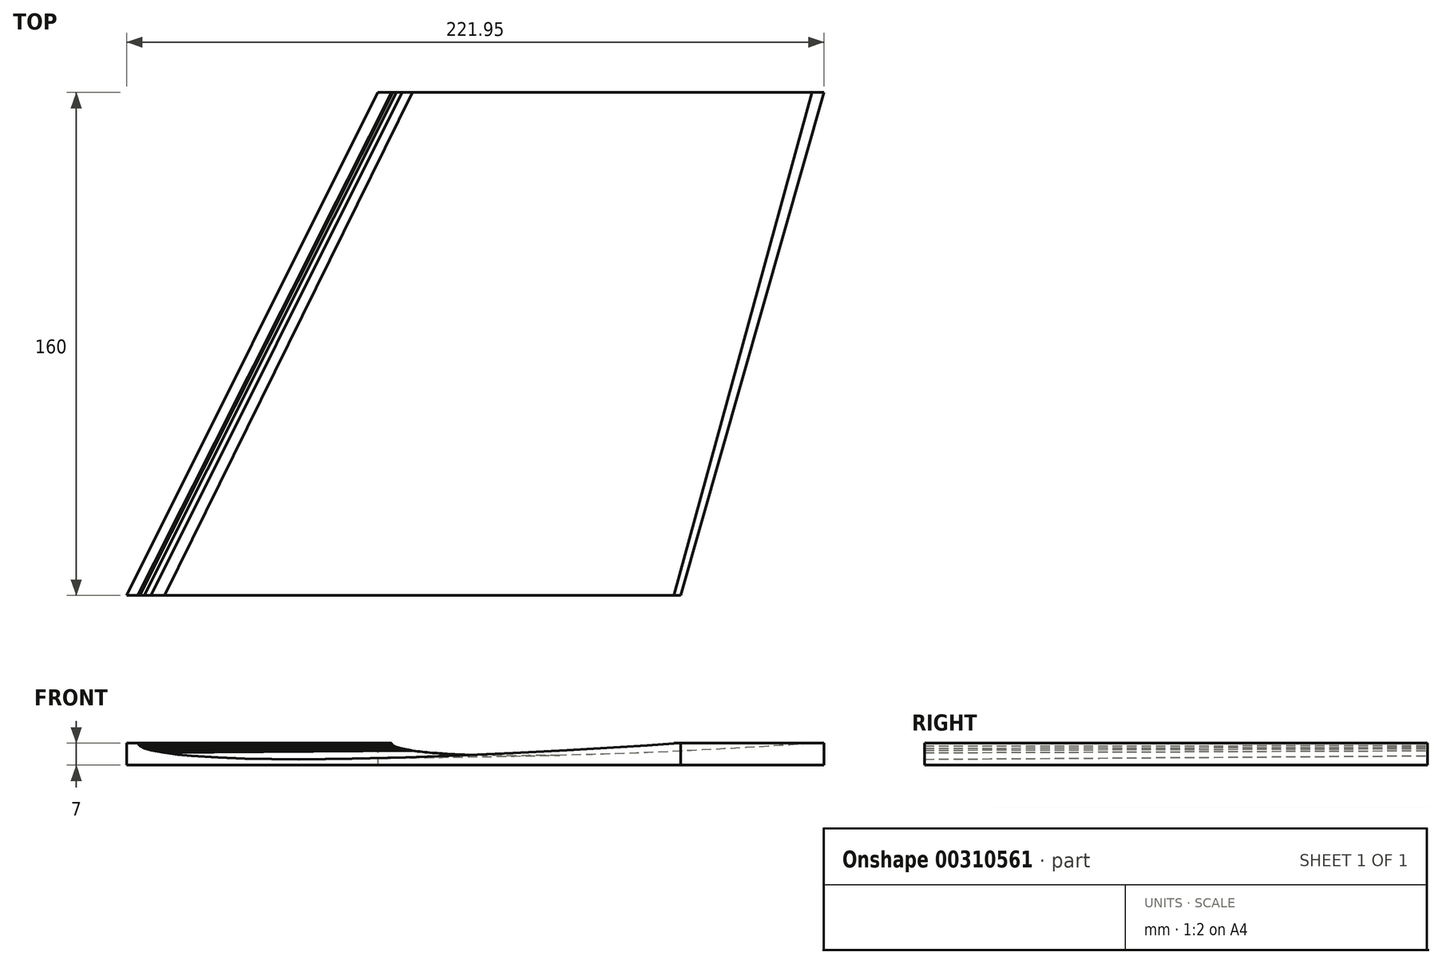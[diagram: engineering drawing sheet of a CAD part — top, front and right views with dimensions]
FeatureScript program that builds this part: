
annotation { "Feature Type Name" : "Feature", "Feature Type Description" : "" }
export const myFeature = defineFeature(function(context is Context, id is Id, definition is map)
    precondition{}
    {
        {
            var Q0;
            Q0=qCreatedBy(makeId("Front.planeOp"),FACE);
            cPlane(context, id + "F0", {"entities" : qUnion([Q0]), "cplaneType" : CPlaneType.OFFSET, "offset" : 242 * mm, "oppositeDirection" : true, "width" : 150 * mm, "height" : 150 * mm});
        }
        {
            var Q0;
            Q0=qCreatedBy(makeId("Front.planeOp"),FACE);
            cPlane(context, id + "F1", {"entities" : qUnion([Q0]), "cplaneType" : CPlaneType.OFFSET, "offset" : 315 * mm, "oppositeDirection" : true, "width" : 150 * mm, "height" : 150 * mm});
        }
        {
            var Q0;
            Q0=qCreatedBy(makeId("Front.planeOp"),FACE);
            var sketch = newSketch(context, id + "F2", { "sketchPlane" : qUnion([Q0])});
            skLineSegment(sketch, "E0", {"start": v(85.33, 0.1) * mm, "end": v(76.8, 0.69) * mm});
            skLineSegment(sketch, "E1", {"start": v(76.8, 0.69) * mm, "end": v(68.27, 1.23) * mm});
            skLineSegment(sketch, "E2", {"start": v(68.27, 1.23) * mm, "end": v(51.2, 2.24) * mm});
            skLineSegment(sketch, "E3", {"start": v(51.2, 2.24) * mm, "end": v(34.13, 3.12) * mm});
            skLineSegment(sketch, "E4", {"start": v(34.13, 3.12) * mm, "end": v(17.07, 3.9) * mm});
            skLineSegment(sketch, "E5", {"start": v(17.07, 3.9) * mm, "end": v(0, 4.51) * mm});
            skLineSegment(sketch, "E6", {"start": v(0, 4.51) * mm, "end": v(-17.07, 4.95) * mm});
            skLineSegment(sketch, "E7", {"start": v(-17.07, 4.95) * mm, "end": v(-34.13, 5.12) * mm});
            skLineSegment(sketch, "E8", {"start": v(-34.13, 5.12) * mm, "end": v(-42.67, 5.07) * mm});
            skLineSegment(sketch, "E9", {"start": v(-42.67, 5.07) * mm, "end": v(-51.2, 4.9) * mm});
            skLineSegment(sketch, "E10", {"start": v(-51.2, 4.9) * mm, "end": v(-59.73, 4.56) * mm});
            skLineSegment(sketch, "E11", {"start": v(-59.73, 4.56) * mm, "end": v(-68.27, 4) * mm});
            skLineSegment(sketch, "E12", {"start": v(-68.27, 4) * mm, "end": v(-72.53, 3.58) * mm});
            skLineSegment(sketch, "E13", {"start": v(-72.53, 3.58) * mm, "end": v(-76.8, 3.03) * mm});
            skLineSegment(sketch, "E14", {"start": v(-76.8, 3.03) * mm, "end": v(-81.07, 2.23) * mm});
            skLineSegment(sketch, "E15", {"start": v(-81.07, 2.23) * mm, "end": v(-83.2, 1.62) * mm});
            skLineSegment(sketch, "E16", {"start": v(-83.2, 1.62) * mm, "end": v(-84.61, 0.9) * mm});
            skLineSegment(sketch, "E17", {"start": v(-84.61, 0.9) * mm, "end": v(-85.33, 0) * mm});
            skLineSegment(sketch, "E18", {"start": v(-85.33, 0) * mm, "end": v(-84.68, -0.91) * mm});
            skLineSegment(sketch, "E19", {"start": v(-84.68, -0.91) * mm, "end": v(-83.2, -1.62) * mm});
            skLineSegment(sketch, "E20", {"start": v(-83.2, -1.62) * mm, "end": v(-81.07, -2.23) * mm});
            skLineSegment(sketch, "E21", {"start": v(-81.07, -2.23) * mm, "end": v(-76.8, -3.03) * mm});
            skLineSegment(sketch, "E22", {"start": v(-76.8, -3.03) * mm, "end": v(-72.53, -3.58) * mm});
            skLineSegment(sketch, "E23", {"start": v(-72.53, -3.58) * mm, "end": v(-68.27, -4) * mm});
            skLineSegment(sketch, "E24", {"start": v(-68.27, -4) * mm, "end": v(-59.73, -4.56) * mm});
            skLineSegment(sketch, "E25", {"start": v(-59.73, -4.56) * mm, "end": v(-51.2, -4.9) * mm});
            skLineSegment(sketch, "E26", {"start": v(-51.2, -4.9) * mm, "end": v(-42.67, -5.07) * mm});
            skLineSegment(sketch, "E27", {"start": v(-42.67, -5.07) * mm, "end": v(-34.13, -5.12) * mm});
            skLineSegment(sketch, "E28", {"start": v(-34.13, -5.12) * mm, "end": v(-17.07, -4.95) * mm});
            skLineSegment(sketch, "E29", {"start": v(-17.07, -4.95) * mm, "end": v(0, -4.51) * mm});
            skLineSegment(sketch, "E30", {"start": v(0, -4.51) * mm, "end": v(17.07, -3.9) * mm});
            skLineSegment(sketch, "E31", {"start": v(17.07, -3.9) * mm, "end": v(34.13, -3.12) * mm});
            skLineSegment(sketch, "E32", {"start": v(34.13, -3.12) * mm, "end": v(51.2, -2.24) * mm});
            skLineSegment(sketch, "E33", {"start": v(51.2, -2.24) * mm, "end": v(68.27, -1.23) * mm});
            skLineSegment(sketch, "E34", {"start": v(68.27, -1.23) * mm, "end": v(76.8, -0.69) * mm});
            skLineSegment(sketch, "E35", {"start": v(76.8, -0.69) * mm, "end": v(85.33, -0.1) * mm});
            skLineSegment(sketch, "E36", {"start": v(85.33, -0.1) * mm, "end": v(85.33, 0.1) * mm});
            skSolve(sketch);
        }
        {
            var Q0;
            Q0=qCreatedBy(id+"F0.planeOp",FACE);
            var sketch = newSketch(context, id + "F3", { "sketchPlane" : qUnion([Q0])});
            skLineSegment(sketch, "E37", {"start": v(151.77, 0.06) * mm, "end": v(146.02, 0.44) * mm});
            skLineSegment(sketch, "E38", {"start": v(146.02, 0.44) * mm, "end": v(140.27, 0.8) * mm});
            skLineSegment(sketch, "E39", {"start": v(140.27, 0.8) * mm, "end": v(128.77, 1.48) * mm});
            skLineSegment(sketch, "E40", {"start": v(128.77, 1.48) * mm, "end": v(117.27, 2.07) * mm});
            skLineSegment(sketch, "E41", {"start": v(117.27, 2.07) * mm, "end": v(105.77, 2.58) * mm});
            skLineSegment(sketch, "E42", {"start": v(105.77, 2.58) * mm, "end": v(94.27, 3) * mm});
            skLineSegment(sketch, "E43", {"start": v(94.27, 3) * mm, "end": v(82.77, 3.28) * mm});
            skLineSegment(sketch, "E44", {"start": v(82.77, 3.28) * mm, "end": v(71.27, 3.4) * mm});
            skLineSegment(sketch, "E45", {"start": v(71.27, 3.4) * mm, "end": v(65.52, 3.36) * mm});
            skLineSegment(sketch, "E46", {"start": v(65.52, 3.36) * mm, "end": v(59.77, 3.24) * mm});
            skLineSegment(sketch, "E47", {"start": v(59.77, 3.24) * mm, "end": v(54.02, 3.02) * mm});
            skLineSegment(sketch, "E48", {"start": v(54.02, 3.02) * mm, "end": v(48.27, 2.64) * mm});
            skLineSegment(sketch, "E49", {"start": v(48.27, 2.64) * mm, "end": v(45.4, 2.37) * mm});
            skLineSegment(sketch, "E50", {"start": v(45.4, 2.37) * mm, "end": v(42.52, 2) * mm});
            skLineSegment(sketch, "E51", {"start": v(42.52, 2) * mm, "end": v(39.65, 1.47) * mm});
            skLineSegment(sketch, "E52", {"start": v(39.65, 1.47) * mm, "end": v(38.2, 1.06) * mm});
            skLineSegment(sketch, "E53", {"start": v(38.2, 1.06) * mm, "end": v(37.26, 0.58) * mm});
            skLineSegment(sketch, "E54", {"start": v(37.26, 0.58) * mm, "end": v(36.77, -0.01) * mm});
            skLineSegment(sketch, "E55", {"start": v(36.77, -0.01) * mm, "end": v(37.21, -0.62) * mm});
            skLineSegment(sketch, "E56", {"start": v(37.21, -0.62) * mm, "end": v(38.2, -1.09) * mm});
            skLineSegment(sketch, "E57", {"start": v(38.2, -1.09) * mm, "end": v(39.65, -1.5) * mm});
            skLineSegment(sketch, "E58", {"start": v(39.65, -1.5) * mm, "end": v(42.52, -2.03) * mm});
            skLineSegment(sketch, "E59", {"start": v(42.52, -2.03) * mm, "end": v(45.4, -2.4) * mm});
            skLineSegment(sketch, "E60", {"start": v(45.4, -2.4) * mm, "end": v(48.27, -2.67) * mm});
            skLineSegment(sketch, "E61", {"start": v(48.27, -2.67) * mm, "end": v(54.02, -3.05) * mm});
            skLineSegment(sketch, "E62", {"start": v(54.02, -3.05) * mm, "end": v(59.77, -3.27) * mm});
            skLineSegment(sketch, "E63", {"start": v(59.77, -3.27) * mm, "end": v(65.52, -3.38) * mm});
            skLineSegment(sketch, "E64", {"start": v(65.52, -3.38) * mm, "end": v(71.27, -3.42) * mm});
            skLineSegment(sketch, "E65", {"start": v(71.27, -3.42) * mm, "end": v(82.77, -3.3) * mm});
            skLineSegment(sketch, "E66", {"start": v(82.77, -3.3) * mm, "end": v(94.27, -3.02) * mm});
            skLineSegment(sketch, "E67", {"start": v(94.27, -3.02) * mm, "end": v(105.77, -2.6) * mm});
            skLineSegment(sketch, "E68", {"start": v(105.77, -2.6) * mm, "end": v(117.27, -2.1) * mm});
            skLineSegment(sketch, "E69", {"start": v(117.27, -2.1) * mm, "end": v(128.77, -1.5) * mm});
            skLineSegment(sketch, "E70", {"start": v(128.77, -1.5) * mm, "end": v(140.27, -0.83) * mm});
            skLineSegment(sketch, "E71", {"start": v(140.27, -0.83) * mm, "end": v(146.02, -0.47) * mm});
            skLineSegment(sketch, "E72", {"start": v(146.02, -0.47) * mm, "end": v(151.77, -0.08) * mm});
            skLineSegment(sketch, "E73", {"start": v(151.77, -0.08) * mm, "end": v(151.77, 0.06) * mm});
            skSolve(sketch);
        }
        {
            var Q0;
            Q0=qCreatedBy(id+"F1.planeOp",FACE);
            var sketch = newSketch(context, id + "F4", { "sketchPlane" : qUnion([Q0])});
            skLineSegment(sketch, "E74", {"start": v(172.88, 0.04) * mm, "end": v(169.63, 0.25) * mm});
            skLineSegment(sketch, "E75", {"start": v(169.63, 0.25) * mm, "end": v(166.37, 0.45) * mm});
            skLineSegment(sketch, "E76", {"start": v(166.37, 0.45) * mm, "end": v(159.87, 0.82) * mm});
            skLineSegment(sketch, "E77", {"start": v(159.87, 0.82) * mm, "end": v(153.36, 1.14) * mm});
            skLineSegment(sketch, "E78", {"start": v(153.36, 1.14) * mm, "end": v(146.85, 1.42) * mm});
            skLineSegment(sketch, "E79", {"start": v(146.85, 1.42) * mm, "end": v(140.34, 1.65) * mm});
            skLineSegment(sketch, "E80", {"start": v(140.34, 1.65) * mm, "end": v(133.83, 1.8) * mm});
            skLineSegment(sketch, "E81", {"start": v(133.83, 1.8) * mm, "end": v(127.33, 1.87) * mm});
            skLineSegment(sketch, "E82", {"start": v(127.33, 1.87) * mm, "end": v(124.07, 1.85) * mm});
            skLineSegment(sketch, "E83", {"start": v(124.07, 1.85) * mm, "end": v(120.82, 1.79) * mm});
            skLineSegment(sketch, "E84", {"start": v(120.82, 1.79) * mm, "end": v(117.56, 1.67) * mm});
            skLineSegment(sketch, "E85", {"start": v(117.56, 1.67) * mm, "end": v(114.31, 1.46) * mm});
            skLineSegment(sketch, "E86", {"start": v(114.31, 1.46) * mm, "end": v(112.68, 1.3) * mm});
            skLineSegment(sketch, "E87", {"start": v(112.68, 1.3) * mm, "end": v(111.06, 1.1) * mm});
            skLineSegment(sketch, "E88", {"start": v(111.06, 1.1) * mm, "end": v(109.43, 0.81) * mm});
            skLineSegment(sketch, "E89", {"start": v(109.43, 0.81) * mm, "end": v(108.62, 0.6) * mm});
            skLineSegment(sketch, "E90", {"start": v(108.62, 0.6) * mm, "end": v(108.08, 0.33) * mm});
            skLineSegment(sketch, "E91", {"start": v(108.2, 0.47) * mm, "end": v(107.8, 0) * mm});
            skLineSegment(sketch, "E92", {"start": v(107.8, 0) * mm, "end": v(108.05, -0.33) * mm});
            skLineSegment(sketch, "E93", {"start": v(108.05, -0.33) * mm, "end": v(108.62, -0.6) * mm});
            skLineSegment(sketch, "E94", {"start": v(108.62, -0.6) * mm, "end": v(109.43, -0.81) * mm});
            skLineSegment(sketch, "E95", {"start": v(109.43, -0.81) * mm, "end": v(111.06, -1.1) * mm});
            skLineSegment(sketch, "E96", {"start": v(111.06, -1.1) * mm, "end": v(112.68, -1.3) * mm});
            skLineSegment(sketch, "E97", {"start": v(112.68, -1.3) * mm, "end": v(114.31, -1.46) * mm});
            skLineSegment(sketch, "E98", {"start": v(114.31, -1.46) * mm, "end": v(117.56, -1.67) * mm});
            skLineSegment(sketch, "E99", {"start": v(117.56, -1.67) * mm, "end": v(120.82, -1.79) * mm});
            skLineSegment(sketch, "E100", {"start": v(120.82, -1.79) * mm, "end": v(124.07, -1.85) * mm});
            skLineSegment(sketch, "E101", {"start": v(124.07, -1.85) * mm, "end": v(127.33, -1.87) * mm});
            skLineSegment(sketch, "E102", {"start": v(127.33, -1.87) * mm, "end": v(133.83, -1.8) * mm});
            skLineSegment(sketch, "E103", {"start": v(133.83, -1.8) * mm, "end": v(140.34, -1.65) * mm});
            skLineSegment(sketch, "E104", {"start": v(140.34, -1.65) * mm, "end": v(146.85, -1.42) * mm});
            skLineSegment(sketch, "E105", {"start": v(146.85, -1.42) * mm, "end": v(153.36, -1.14) * mm});
            skLineSegment(sketch, "E106", {"start": v(153.36, -1.14) * mm, "end": v(159.87, -0.82) * mm});
            skLineSegment(sketch, "E107", {"start": v(159.87, -0.82) * mm, "end": v(166.37, -0.45) * mm});
            skLineSegment(sketch, "E108", {"start": v(166.37, -0.45) * mm, "end": v(169.63, -0.25) * mm});
            skLineSegment(sketch, "E109", {"start": v(169.63, -0.25) * mm, "end": v(172.88, -0.04) * mm});
            skLineSegment(sketch, "E110", {"start": v(172.88, -0.04) * mm, "end": v(172.88, 0.04) * mm});
            skSolve(sketch);
        }
        {
            var Q0;
            Q0=makeQuery(id+"F2.imprint","IMPRINT",FACE,{"disambiguationData":[TD([[makeQuery(id+"F2.imprint","IMPRINT",EDGE,{"derivedFrom":sQuery(id+"F2.wireOp",EDGE,"E0")}),1.0]])]});
            var Q1;
            Q1=makeQuery(id+"F3.imprint","IMPRINT",FACE,{"disambiguationData":[TD([[makeQuery(id+"F3.imprint","IMPRINT",EDGE,{"derivedFrom":sQuery(id+"F3.wireOp",EDGE,"E37")}),1.0]])]});
            loft(context, id + "F5", {"sheetProfilesArray" : [{ "sheetProfileEntities" : qUnion([Q0]) }, { "sheetProfileEntities" : qUnion([Q1]) }]});
        }
        {
            var Q0;
            Q0=qCreatedBy(makeId("Front.planeOp"),FACE);
            var sketch = newSketch(context, id + "F6", { "sketchPlane" : qUnion([Q0])});
            skLineSegment(sketch, "E111.bottom", {"start": v(-88.87, 0) * mm, "end": v(61.07, 0) * mm});
            skLineSegment(sketch, "E112.bottom", {"start": v(-88.87, 0) * mm, "end": v(87.49, 0) * mm});
            skLineSegment(sketch, "E112.top", {"start": v(-88.87, -7) * mm, "end": v(87.49, -7) * mm});
            skLineSegment(sketch, "E112.left", {"start": v(-88.87, 0) * mm, "end": v(-88.87, -7) * mm});
            skLineSegment(sketch, "E112.right", {"start": v(87.49, 0) * mm, "end": v(87.49, -7) * mm});
            skSolve(sketch);
        }
        {
            var Q0;
            Q0=qCreatedBy(id+"F0.planeOp",FACE);
            var sketch = newSketch(context, id + "F7", { "sketchPlane" : qUnion([Q0])});
            skLineSegment(sketch, "E113.bottom", {"start": v(32, 0) * mm, "end": v(156.45, 0) * mm});
            skLineSegment(sketch, "E113.top", {"start": v(32, -7) * mm, "end": v(156.45, -7) * mm});
            skLineSegment(sketch, "E113.left", {"start": v(32, 0) * mm, "end": v(32, -7) * mm});
            skLineSegment(sketch, "E113.right", {"start": v(156.45, 0) * mm, "end": v(156.45, -7) * mm});
            skSolve(sketch);
        }
        {
            var Q1;
            Q1=qSketchRegion(id+"F3",true);
            var Q2;
            Q2=makeQuery(id+"F4.imprint","IMPRINT",FACE,{"disambiguationData":[TD([[makeQuery(id+"F4.imprint","IMPRINT",EDGE,{"derivedFrom":sQuery(id+"F4.wireOp",EDGE,"E74")}),1.0]])]});
            loft(context, id + "F8", {"operationType" : NewBodyOperationType.ADD, "sheetProfilesArray" : [{ "sheetProfileEntities" : qUnion([Q1]) }, { "sheetProfileEntities" : qUnion([Q2]) }]});
        }
        {
            var Q0;
            Q0=qCreatedBy(id+"F1.planeOp",FACE);
            var sketch = newSketch(context, id + "F9", { "sketchPlane" : qUnion([Q0])});
            skLineSegment(sketch, "E114.bottom", {"start": v(177.22, 0) * mm, "end": v(102.9, 0) * mm});
            skLineSegment(sketch, "E114.top", {"start": v(177.22, -7) * mm, "end": v(102.9, -7) * mm});
            skLineSegment(sketch, "E114.left", {"start": v(177.22, 0) * mm, "end": v(177.22, -7) * mm});
            skLineSegment(sketch, "E114.right", {"start": v(102.9, 0) * mm, "end": v(102.9, -7) * mm});
            skSolve(sketch);
        }
        {
            var Q1;
            Q1=makeQuery(id+"F6.imprint","IMPRINT",FACE,{"disambiguationData":[TD([[makeQuery(id+"F6.imprint","IMPRINT",EDGE,{"derivedFrom":sQuery(id+"F6.wireOp",EDGE,"E112.bottom")}),-1.0]])]});
            var Q2;
            Q2=makeQuery(id+"F7.imprint","IMPRINT",FACE,{"disambiguationData":[TD([[makeQuery(id+"F7.imprint","IMPRINT",EDGE,{"derivedFrom":sQuery(id+"F7.wireOp",EDGE,"E113.bottom")}),-1.0]])]});
            loft(context, id + "F10", {"sheetProfilesArray" : [{ "sheetProfileEntities" : qUnion([Q1]) }, { "sheetProfileEntities" : qUnion([Q2]) }]});
        }
        {
            var Q1;
            Q1=makeQuery(id+"F9.imprint","IMPRINT",FACE,{"disambiguationData":[TD([[makeQuery(id+"F9.imprint","IMPRINT",EDGE,{"derivedFrom":sQuery(id+"F9.wireOp",EDGE,"E114.top")}),-1.0]])]});
            var Q2;
            Q2=makeQuery(id+"F7.imprint","IMPRINT",FACE,{"disambiguationData":[TD([[makeQuery(id+"F7.imprint","IMPRINT",EDGE,{"derivedFrom":sQuery(id+"F7.wireOp",EDGE,"E113.bottom")}),-1.0]])]});
            loft(context, id + "F11", {"sheetProfilesArray" : [{ "sheetProfileEntities" : qUnion([Q1]) }, { "sheetProfileEntities" : qUnion([Q2]) }]});
        }
        {
            var Q0;
            Q0=makeQuery(id+"F5.opLoft","SWEPT_BODY",BODY,{"disambiguationData":[OSD([makeQuery(id+"F2.imprint","IMPRINT",FACE,{"disambiguationData":[TD([[makeQuery(id+"F2.imprint","IMPRINT",EDGE,{"derivedFrom":sQuery(id+"F2.wireOp",EDGE,"E0")}),1.0]])]}),makeQuery(id+"F3.imprint","IMPRINT",FACE,{"disambiguationData":[TD([[makeQuery(id+"F3.imprint","IMPRINT",EDGE,{"derivedFrom":sQuery(id+"F3.wireOp",EDGE,"E37")}),1.0]])]})])]});
            var Q1;
            Q1=makeQuery(id+"F10.opLoft","SWEPT_BODY",BODY,{"disambiguationData":[OSD([makeQuery(id+"F6.imprint","IMPRINT",FACE,{"disambiguationData":[TD([[makeQuery(id+"F6.imprint","IMPRINT",EDGE,{"derivedFrom":sQuery(id+"F6.wireOp",EDGE,"E112.bottom")}),-1.0]])]}),makeQuery(id+"F7.imprint","IMPRINT",FACE,{"disambiguationData":[TD([[makeQuery(id+"F7.imprint","IMPRINT",EDGE,{"derivedFrom":sQuery(id+"F7.wireOp",EDGE,"E113.bottom")}),-1.0]])]})])]});
            booleanBodies(context, id + "F12", {"operationType" : BooleanOperationType.SUBTRACTION, "tools" : qUnion([Q0]), "targets" : qUnion([Q1])});
        }
        {
            var Q0;
            Q0=qCreatedBy(makeId("Front.planeOp"),FACE);
            cPlane(context, id + "F13", {"entities" : qUnion([Q0]), "cplaneType" : CPlaneType.OFFSET, "offset" : 160 * mm, "oppositeDirection" : true, "width" : 150 * mm, "height" : 150 * mm});
        }
        {
            var Q0;
            Q0=qCreatedBy(id+"F13.planeOp",FACE);
            var sketch = newSketch(context, id + "F14", { "sketchPlane" : qUnion([Q0])});
            skLineSegment(sketch, "E115.bottom", {"start": v(-91.18, 11.32) * mm, "end": v(184.82, 11.32) * mm});
            skLineSegment(sketch, "E115.top", {"start": v(-91.18, -19.62) * mm, "end": v(184.82, -19.62) * mm});
            skLineSegment(sketch, "E115.left", {"start": v(-91.18, 11.32) * mm, "end": v(-91.18, -19.62) * mm});
            skLineSegment(sketch, "E115.right", {"start": v(184.82, 11.32) * mm, "end": v(184.82, -19.62) * mm});
            skSolve(sketch);
        }
        {
            var Q0;
            Q0=makeQuery(id+"F14.imprint","IMPRINT",FACE,{"disambiguationData":[TD([[makeQuery(id+"F14.imprint","IMPRINT",EDGE,{"derivedFrom":sQuery(id+"F14.wireOp",EDGE,"E115.bottom")}),-1.0]])]});
            extrude(context, id + "F15", {"entities" : qUnion([Q0]), "operationType" : NewBodyOperationType.REMOVE, "oppositeDirection" : true, "depth" : 200 * mm});
        }
    });
